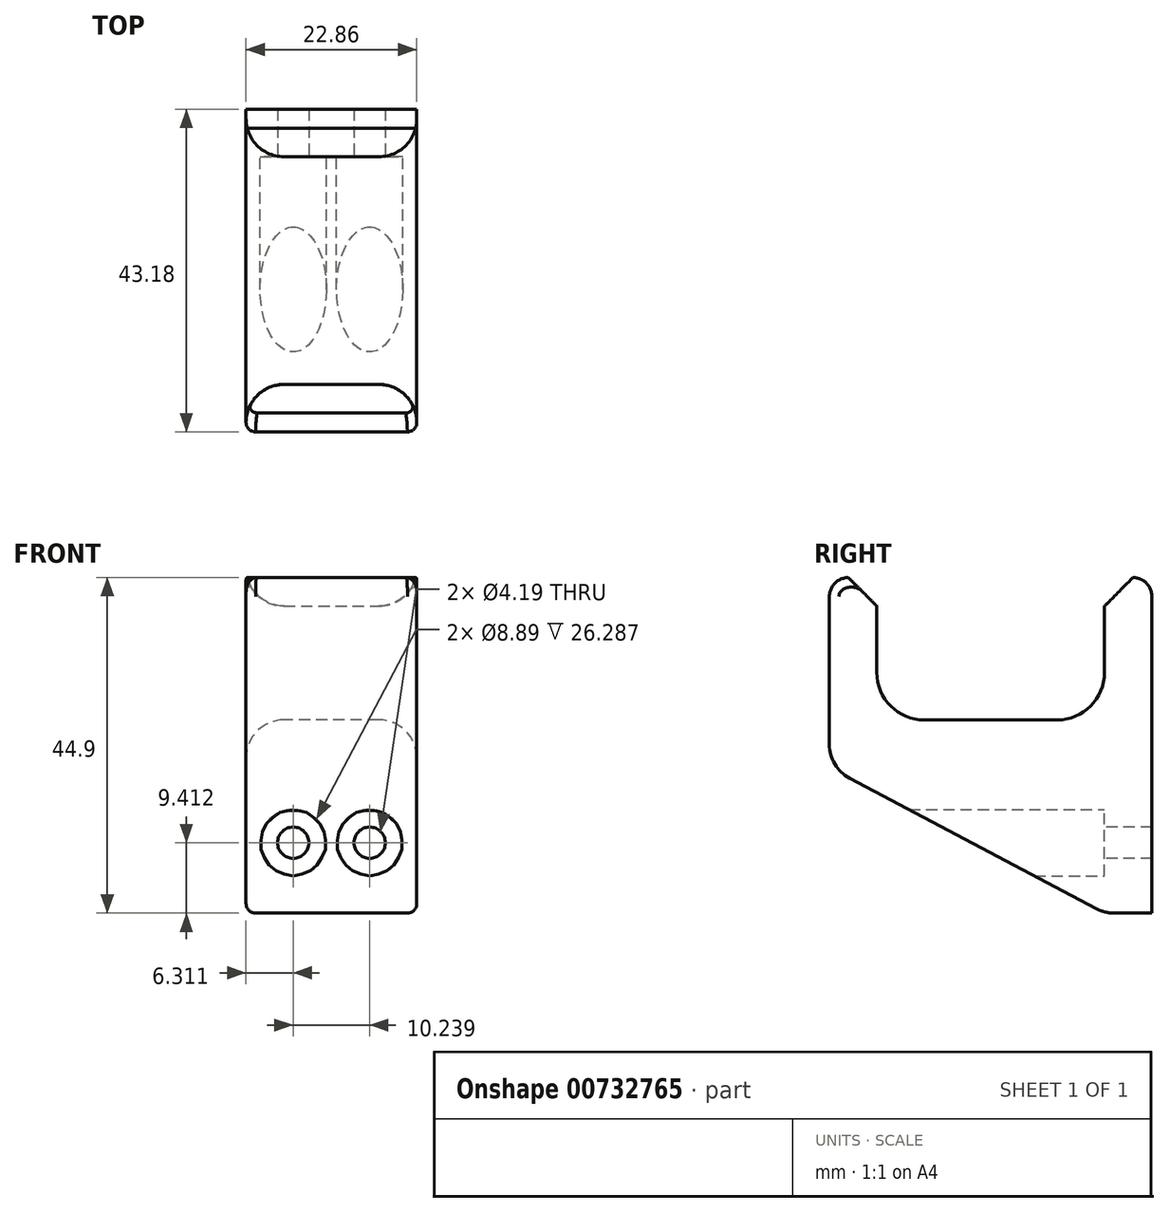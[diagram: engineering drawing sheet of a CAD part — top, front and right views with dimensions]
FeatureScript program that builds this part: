
annotation { "Feature Type Name" : "Feature", "Feature Type Description" : "" }
export const myFeature = defineFeature(function(context is Context, id is Id, definition is map)
    precondition{}
    {
        {
            var Q0;
            Q0=qCreatedBy(makeId("Right.planeOp"),FACE);
            var sketch = newSketch(context, id + "F0", { "sketchPlane" : qUnion([Q0])});
            skLineSegment(sketch, "E0", {"start": v(0, 6.35) * mm, "end": v(15.24, 6.35) * mm});
            skLineSegment(sketch, "E1", {"start": v(15.24, 6.35) * mm, "end": v(15.24, 25.4) * mm});
            skLineSegment(sketch, "E2", {"start": v(15.24, 25.4) * mm, "end": v(21.59, 25.4) * mm});
            skLineSegment(sketch, "E3", {"start": v(21.59, 25.4) * mm, "end": v(21.6, 0) * mm});
            skLineSegment(sketch, "E4", {"start": v(21.59, 0) * mm, "end": v(21.59, -19.5) * mm});
            skLineSegment(sketch, "E5", {"start": v(21.6, -19.5) * mm, "end": v(15.24, -19.5) * mm});
            skLineSegment(sketch, "E6", {"start": v(15.24, -19.5) * mm, "end": v(-21.59, 0) * mm});
            skLineSegment(sketch, "E7", {"start": v(-21.6, 0) * mm, "end": v(-21.6, 25.4) * mm});
            skLineSegment(sketch, "E8", {"start": v(-21.6, 25.4) * mm, "end": v(-15.24, 25.4) * mm});
            skLineSegment(sketch, "E9", {"start": v(-15.24, 25.4) * mm, "end": v(-15.24, 6.35) * mm});
            skLineSegment(sketch, "E10", {"start": v(-15.24, 6.35) * mm, "end": v(0, 6.35) * mm});
            skSolve(sketch);
        }
        {
            var Q0;
            Q0 = qSketchRegion(id + "F0", true);
            extrude(context, id + "F1", {"entities" : qUnion([Q0]), "endBound" : BoundingType.SYMMETRIC, "depth" : 22.86 * mm, "offsetDistance" : 25.4 * mm});
        }
        {
            var Q0;
            Q0=qCreatedBy(makeId("Front.planeOp"),FACE);
            var sketch = newSketch(context, id + "F2", { "sketchPlane" : qUnion([Q0])});
            skCircle(sketch, "E11", {"center": v(-5.12, -10.09) * mm, "radius": 2.1 * mm});
            skCircle(sketch, "E12.MirrorC", {"center": v(5.12, -10.09) * mm, "radius": 2.1 * mm});
            skSolve(sketch);
        }
        {
            var Q0;
            Q0 = qSketchRegion(id + "F2", true);
            extrude(context, id + "F3", {"entities" : qUnion([Q0]), "operationType" : NewBodyOperationType.REMOVE, "endBound" : BoundingType.SYMMETRIC, "oppositeDirection" : true, "depth" : 50.8 * mm, "offsetDistance" : 25.4 * mm});
        }
        {
            var Q0;
            Q0=makeQuery(id+"F1.opExtrude","SWEPT_FACE",FACE,{"disambiguationData":[OSD([sQuery(id+"F0.wireOp",EDGE,"E1")])]});
            var sketch = newSketch(context, id + "F4", { "sketchPlane" : qUnion([Q0])});
            skCircle(sketch, "E13", {"center": v(-5.12, -10.09) * mm, "radius": 4.45 * mm});
            skCircle(sketch, "E14.MirrorC", {"center": v(5.12, -10.09) * mm, "radius": 4.45 * mm});
            skSolve(sketch);
        }
        {
            var Q0;
            Q0 = qSketchRegion(id + "F4", true);
            extrude(context, id + "F5", {"entities" : qUnion([Q0]), "operationType" : NewBodyOperationType.REMOVE, "endBound" : BoundingType.THROUGH_ALL, "depth" : 25.4 * mm, "offsetDistance" : 25.4 * mm});
        }
        {
            var Q0;
            Q0=makeQuery(id+"F1.opExtrude","SWEPT_EDGE",EDGE,{"disambiguationData":[OSD([sQuery(id+"F0.wireOp",EDGE,"E0"),sQuery(id+"F0.wireOp",EDGE,"E1")])]});
            var Q1;
            Q1=makeQuery(id+"F1.opExtrude","SWEPT_EDGE",EDGE,{"disambiguationData":[OSD([sQuery(id+"F0.wireOp",EDGE,"E9"),sQuery(id+"F0.wireOp",EDGE,"E10")])]});
            fillet(context, id + "F6", {"entities" : qUnion([Q0, Q1]), "radius" : 6.35 * mm, "tangentPropagation" : true, "allowEdgeOverflow" : false});
        }
        {
            var Q0;
            Q0=makeQuery(id+"F1.opExtrude","SWEPT_EDGE",EDGE,{"disambiguationData":[OSD([sQuery(id+"F0.wireOp",EDGE,"E1"),sQuery(id+"F0.wireOp",EDGE,"E2")])]});
            var Q1;
            Q1=makeQuery(id+"F1.opExtrude","SWEPT_EDGE",EDGE,{"disambiguationData":[OSD([sQuery(id+"F0.wireOp",EDGE,"E8"),sQuery(id+"F0.wireOp",EDGE,"E9")])]});
            chamfer(context, id + "F7", {"entities" : qUnion([Q0, Q1]), "width" : 3.8 * mm, "tangentPropagation" : true});
        }
        {
            var Q0;
            Q0=makeQuery(id+"F1.opExtrude","SWEPT_EDGE",EDGE,{"disambiguationData":[OSD([sQuery(id+"F0.wireOp",EDGE,"E7"),sQuery(id+"F0.wireOp",EDGE,"E8")])]});
            var Q1;
            Q1=makeQuery(id+"F1.opExtrude","SWEPT_EDGE",EDGE,{"disambiguationData":[OSD([sQuery(id+"F0.wireOp",EDGE,"E2"),sQuery(id+"F0.wireOp",EDGE,"E3")])]});
            fillet(context, id + "F8", {"entities" : qUnion([Q0, Q1]), "radius" : 2.54 * mm, "tangentPropagation" : true, "allowEdgeOverflow" : false});
        }
        {
            var Q0;
            Q0=makeQuery(id+"F1.opExtrude","CAP_EDGE",EDGE,{"disambiguationData":[OSD([sQuery(id+"F0.wireOp",EDGE,"E0"),sQuery(id+"F0.wireOp",EDGE,"E10")])],"isStart":false});
            var Q1;
            {var subQ0=sQuery(id+"F0.wireOp",EDGE,"E1");var subQ1=sQuery(id+"F0.wireOp",EDGE,"E0");Q1=makeQuery(id+"F6.opFillet","BLEND_EDGE",EDGE,{"blendedFrom":[makeQuery(id+"F1.opExtrude","SWEPT_EDGE",EDGE,{"disambiguationData":[OSD([subQ1,subQ0])]}),makeQuery(id+"F1.opExtrude","CAP_FACE",FACE,{"disambiguationData":[OSD([subQ1,subQ0,sQuery(id+"F0.wireOp",EDGE,"E2"),sQuery(id+"F0.wireOp",EDGE,"E3"),sQuery(id+"F0.wireOp",EDGE,"E4"),sQuery(id+"F0.wireOp",EDGE,"E5"),sQuery(id+"F0.wireOp",EDGE,"E6"),sQuery(id+"F0.wireOp",EDGE,"E7"),sQuery(id+"F0.wireOp",EDGE,"E8"),sQuery(id+"F0.wireOp",EDGE,"E9"),sQuery(id+"F0.wireOp",EDGE,"E10")])],"isStart":true})],"blendedInto":[makeQuery(id+"F1.opExtrude","CAP_FACE",FACE,{"disambiguationData":[OSD([subQ1,subQ0,sQuery(id+"F0.wireOp",EDGE,"E2"),sQuery(id+"F0.wireOp",EDGE,"E3"),sQuery(id+"F0.wireOp",EDGE,"E4"),sQuery(id+"F0.wireOp",EDGE,"E5"),sQuery(id+"F0.wireOp",EDGE,"E6"),sQuery(id+"F0.wireOp",EDGE,"E7"),sQuery(id+"F0.wireOp",EDGE,"E8"),sQuery(id+"F0.wireOp",EDGE,"E9"),sQuery(id+"F0.wireOp",EDGE,"E10")])],"isStart":true})]});}
            var Q2;
            Q2=makeQuery(id+"F1.opExtrude","SWEPT_EDGE",EDGE,{"disambiguationData":[OSD([sQuery(id+"F0.wireOp",EDGE,"E6"),sQuery(id+"F0.wireOp",EDGE,"E7")])]});
            var Q3;
            Q3=makeQuery(id+"F1.opExtrude","SWEPT_EDGE",EDGE,{"disambiguationData":[OSD([sQuery(id+"F0.wireOp",EDGE,"E5"),sQuery(id+"F0.wireOp",EDGE,"E6")])]});
            fillet(context, id + "F9", {"entities" : qUnion([Q0, Q1, Q2, Q3]), "radius" : 5.08 * mm, "tangentPropagation" : true, "allowEdgeOverflow" : false});
        }
        {
            var Q0;
            Q0=makeQuery(id+"F1.opExtrude","CAP_EDGE",EDGE,{"disambiguationData":[OSD([sQuery(id+"F0.wireOp",EDGE,"E6")])],"isStart":false});
            var Q1;
            Q1=makeQuery(id+"F1.opExtrude","CAP_EDGE",EDGE,{"disambiguationData":[OSD([sQuery(id+"F0.wireOp",EDGE,"E7")])],"isStart":true});
            fillet(context, id + "F10", {"entities" : qUnion([Q0, Q1]), "radius" : 1.27 * mm, "tangentPropagation" : true, "allowEdgeOverflow" : false});
        }
    });
